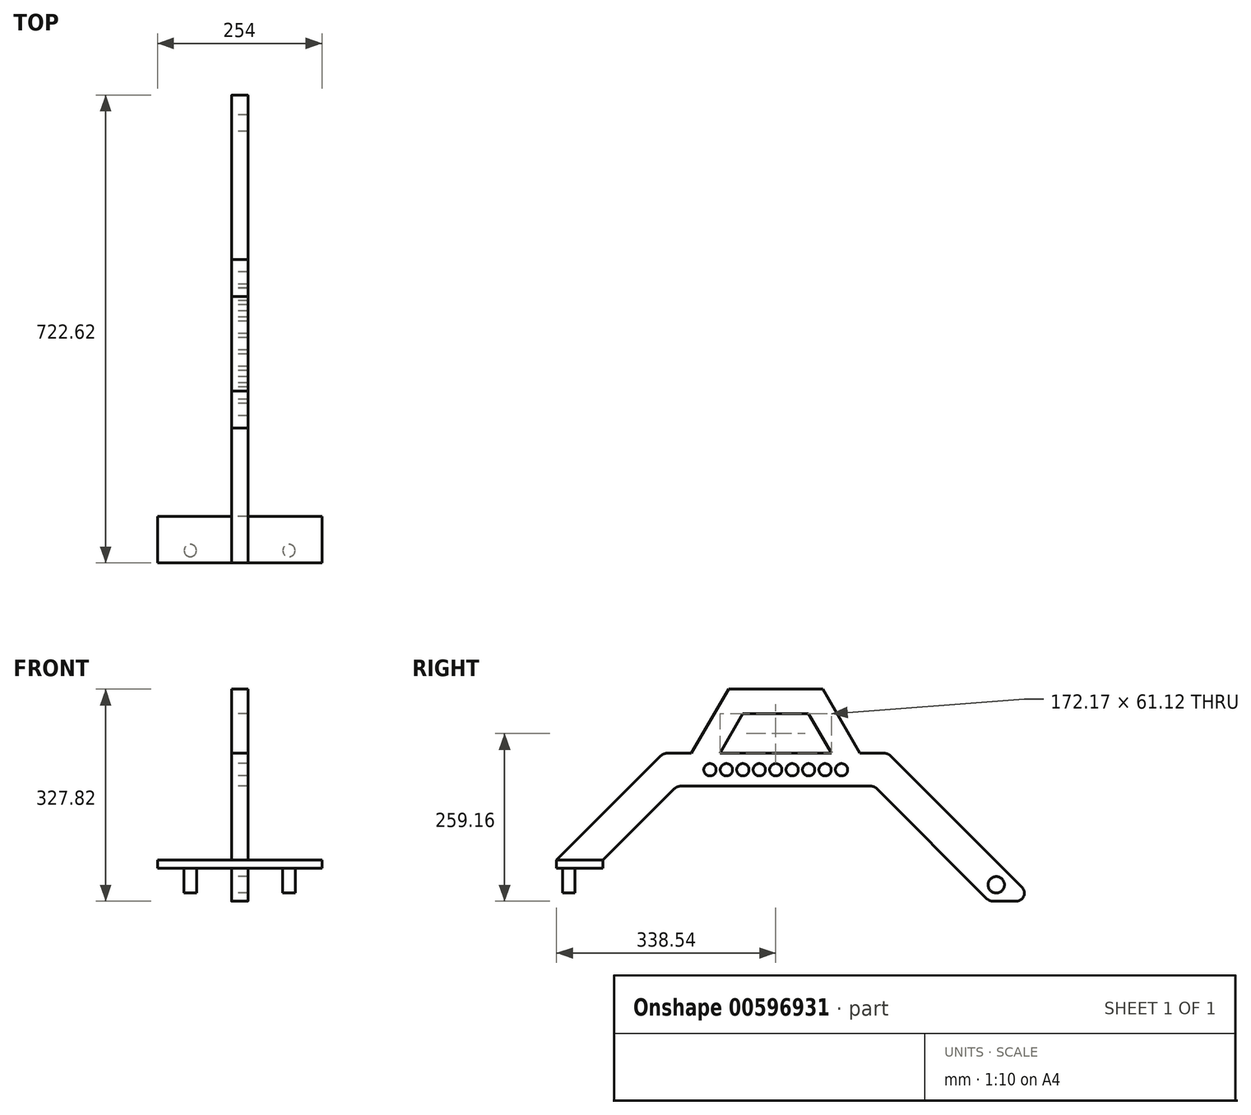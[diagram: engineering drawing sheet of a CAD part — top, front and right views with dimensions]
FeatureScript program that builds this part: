
annotation { "Feature Type Name" : "Feature", "Feature Type Description" : "" }
export const myFeature = defineFeature(function(context is Context, id is Id, definition is map)
    precondition{}
    {
        {
            var Q0;
            Q0=qCreatedBy(makeId("Right.planeOp"),FACE);
            var sketch = newSketch(context, id + "F0", { "sketchPlane" : qUnion([Q0])});
            skLineSegment(sketch, "E0", {"start": v(0, 0) * mm, "end": v(110.58, 110.58) * mm});
            skLineSegment(sketch, "E1", {"start": v(119.56, 114.3) * mm, "end": v(413.84, 114.3) * mm});
            skLineSegment(sketch, "E2", {"start": v(422.82, 110.58) * mm, "end": v(593.18, -59.78) * mm});
            skLineSegment(sketch, "E3.0", {"start": v(443.86, 161.38) * mm, "end": v(647.06, -41.82) * mm});
            skLineSegment(sketch, "E3.1", {"start": v(98.52, 165.1) * mm, "end": v(136.62, 165.1) * mm});
            skLineSegment(sketch, "E3.2", {"start": v(-71.84, 0) * mm, "end": v(89.54, 161.38) * mm});
            skLineSegment(sketch, "E4", {"start": v(0, 0) * mm, "end": v(-71.84, 0) * mm});
            skLineSegment(sketch, "E5", {"start": v(67.86, 139.7) * mm, "end": v(465.54, 139.7) * mm, "construction": true});
            skLineSegment(sketch, "E6", {"start": v(602.16, -63.5) * mm, "end": v(638.08, -63.5) * mm});
            skCircle(sketch, "E7", {"center": v(165.1, 139.7) * mm, "radius": 9.53 * mm});
            skCircle(sketch, "E8.1.0.0", {"center": v(190.5, 139.7) * mm, "radius": 9.53 * mm});
            skCircle(sketch, "E8.2.0.0", {"center": v(215.9, 139.7) * mm, "radius": 9.53 * mm});
            skCircle(sketch, "E8.3.0.0", {"center": v(241.3, 139.7) * mm, "radius": 9.53 * mm});
            skCircle(sketch, "E8.4.0.0", {"center": v(266.7, 139.7) * mm, "radius": 9.53 * mm});
            skCircle(sketch, "E8.5.0.0", {"center": v(292.1, 139.7) * mm, "radius": 9.53 * mm});
            skCircle(sketch, "E8.6.0.0", {"center": v(317.5, 139.7) * mm, "radius": 9.53 * mm});
            skCircle(sketch, "E8.7.0.0", {"center": v(342.9, 139.7) * mm, "radius": 9.53 * mm});
            skCircle(sketch, "E8.8.0.0", {"center": v(368.3, 139.7) * mm, "radius": 9.53 * mm});
            skLineSegment(sketch, "E8.direction1", {"start": v(165.1, 139.7) * mm, "end": v(190.5, 139.7) * mm, "construction": true});
            skCircle(sketch, "E9", {"center": v(607.42, -38.1) * mm, "radius": 12.7 * mm});
            skLineSegment(sketch, "E10", {"start": v(632.82, -63.5) * mm, "end": v(404.22, 165.1) * mm, "construction": true});
            skPoint(sketch, "E11.visualSharp", {"position": v(668.74, -63.5) * mm});
            skArc(sketch, "E11.filletArc", {"start": v(638.08, -63.5) * mm, "mid": v(649.81, -55.66) * mm, "end": v(647.06, -41.82) * mm});
            skPoint(sketch, "E12.visualSharp", {"position": v(596.9, -63.5) * mm});
            skArc(sketch, "E12.filletArc", {"start": v(593.18, -59.78) * mm, "mid": v(597.3, -62.53) * mm, "end": v(602.16, -63.5) * mm});
            skPoint(sketch, "E13.visualSharp", {"position": v(419.1, 114.3) * mm});
            skArc(sketch, "E13.filletArc", {"start": v(422.82, 110.58) * mm, "mid": v(418.7, 113.33) * mm, "end": v(413.84, 114.3) * mm});
            skPoint(sketch, "E14.visualSharp", {"position": v(440.14, 165.1) * mm});
            skArc(sketch, "E14.filletArc", {"start": v(443.86, 161.38) * mm, "mid": v(439.74, 164.13) * mm, "end": v(434.88, 165.1) * mm});
            skPoint(sketch, "E15.visualSharp", {"position": v(93.26, 165.1) * mm});
            skArc(sketch, "E15.filletArc", {"start": v(98.52, 165.1) * mm, "mid": v(93.66, 164.13) * mm, "end": v(89.54, 161.38) * mm});
            skPoint(sketch, "E16.visualSharp", {"position": v(114.3, 114.3) * mm});
            skArc(sketch, "E16.filletArc", {"start": v(119.56, 114.3) * mm, "mid": v(114.7, 113.33) * mm, "end": v(110.58, 110.58) * mm});
            skLineSegment(sketch, "E17", {"start": v(136.62, 165.1) * mm, "end": v(193.9, 264.32) * mm});
            skLineSegment(sketch, "E18", {"start": v(193.9, 264.32) * mm, "end": v(339.5, 264.32) * mm});
            skLineSegment(sketch, "E19", {"start": v(339.5, 264.32) * mm, "end": v(396.78, 165.1) * mm});
            skLineSegment(sketch, "E20", {"start": v(180.61, 165.1) * mm, "end": v(215.9, 226.22) * mm});
            skLineSegment(sketch, "E21", {"start": v(215.9, 226.22) * mm, "end": v(317.5, 226.22) * mm});
            skLineSegment(sketch, "E22", {"start": v(317.5, 226.22) * mm, "end": v(352.79, 165.1) * mm});
            skLineSegment(sketch, "E23.trimOffspring", {"start": v(180.61, 165.1) * mm, "end": v(352.79, 165.1) * mm});
            skLineSegment(sketch, "E24.trimOffspring", {"start": v(396.78, 165.1) * mm, "end": v(434.88, 165.1) * mm});
            skSolve(sketch);
        }
        {
            var Q0;
            Q0 = qSketchRegion(id + "F0", true);
            extrude(context, id + "F1", {"entities" : qUnion([Q0]), "depth" : 12.7 * mm, "offsetDistance" : 25.4 * mm, "hasSecondDirection" : true, "secondDirectionOppositeDirection" : true, "secondDirectionDepth" : 12.7 * mm});
        }
        {
            var Q0;
            Q0=qCreatedBy(makeId("Top.planeOp"),FACE);
            var sketch = newSketch(context, id + "F2", { "sketchPlane" : qUnion([Q0])});
            skLineSegment(sketch, "E25.bottom", {"start": v(127, 0) * mm, "end": v(-127, 0) * mm});
            skLineSegment(sketch, "E25.top", {"start": v(127, -71.84) * mm, "end": v(-127, -71.84) * mm});
            skLineSegment(sketch, "E25.left", {"start": v(127, 0) * mm, "end": v(127, -71.84) * mm});
            skLineSegment(sketch, "E25.right", {"start": v(-127, 0) * mm, "end": v(-127, -71.84) * mm});
            skSolve(sketch);
        }
        {
            var Q0;
            Q0 = qSketchRegion(id + "F2", true);
            extrude(context, id + "F3", {"entities" : qUnion([Q0]), "operationType" : NewBodyOperationType.ADD, "oppositeDirection" : true, "depth" : 12.7 * mm, "offsetDistance" : 25.4 * mm});
        }
        {
            var Q0;
            Q0=makeQuery(id+"F3.opExtrude","CAP_FACE",FACE,{"disambiguationData":[OSD([sQuery(id+"F2.wireOp",EDGE,"E25.bottom"),sQuery(id+"F2.wireOp",EDGE,"E25.top"),sQuery(id+"F2.wireOp",EDGE,"E25.left"),sQuery(id+"F2.wireOp",EDGE,"E25.right")])],"isStart":false});
            var sketch = newSketch(context, id + "F4", { "sketchPlane" : qUnion([Q0])});
            skCircle(sketch, "E26", {"center": v(76.2, 52.8) * mm, "radius": 9.53 * mm});
            skCircle(sketch, "E27", {"center": v(-76.2, 52.8) * mm, "radius": 9.53 * mm});
            skLineSegment(sketch, "E28", {"start": v(76.2, 52.8) * mm, "end": v(-76.2, 52.8) * mm, "construction": true});
            skPoint(sketch, "E29", {"position": v(0, 52.8) * mm});
            skSolve(sketch);
        }
        {
            var Q0;
            Q0 = qSketchRegion(id + "F4", true);
            extrude(context, id + "F5", {"entities" : qUnion([Q0]), "operationType" : NewBodyOperationType.ADD, "depth" : 38.1 * mm, "offsetDistance" : 25.4 * mm});
        }
    });
